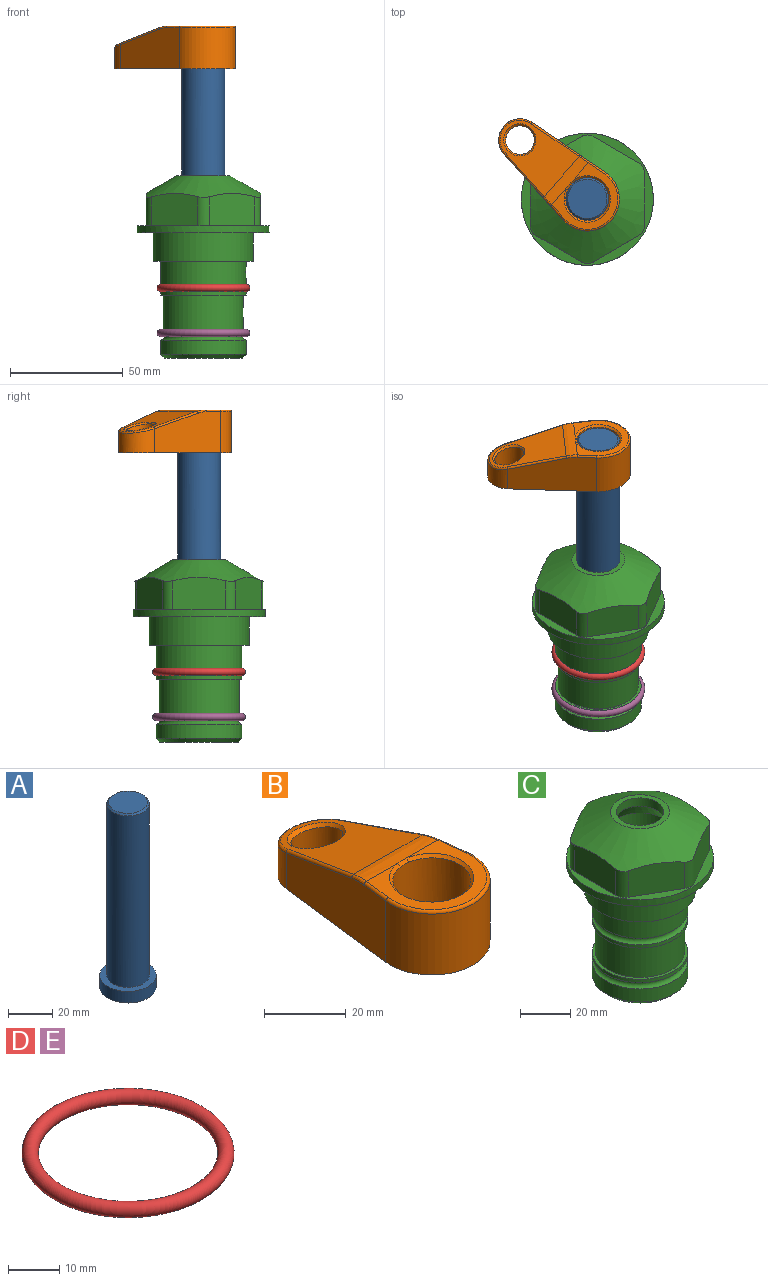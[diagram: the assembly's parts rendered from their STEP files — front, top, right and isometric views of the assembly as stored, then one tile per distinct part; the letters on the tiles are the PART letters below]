
ASSEMBLY  parts=5 mates=4
PART A: 6 faces, bbox 25.4x25.4x101.6 mm
  f0: plane 17.46x17.46mm, normal (0,0,1), area 239.5mm2, adj f5
  f1: plane 25.4x25.4mm, normal (0,0,-1), area 506.7mm2, adj f2
  f2: cylinder r=12.7mm len=25.4mm, axis (0,0,1), area 506.7mm2, adj f1,f3
  f3: plane 25.4x25.4mm, normal (0,0,1), area 221.7mm2, adj f2,f4
  f4: cylinder r=9.53mm len=94.46mm, axis (0,0,1), area 5653mm2, adj f3,f5
  f5: cone r=8.73mm half-angle=45deg, axis (0,0,-1), area 64.4mm2, adj f0,f4
PART B: 31 faces, bbox 31.7x65.5x19.8 mm
  f0: plane 39.12x18.26mm, normal (0.99,0.12,0), area 612.2mm2, adj f1,f4,f7,f11,f13,f15
  f1: cylinder r=9.53mm len=18.91mm, axis (0,0,-1), area 296.1mm2, adj f0,f2,f7,f17
  f2: plane 39.12x18.26mm, normal (-0.99,0.12,0), area 612.2mm2, adj f1,f4,f7,f12,f14,f16
  f3: cylinder r=6.35mm len=12.7mm, axis (0,0,-1), area 362.4mm2, adj f7,f18
  f4: cylinder r=14.29mm len=28.58mm, axis (0,0,-1), area 882.2mm2, adj f0,f2,f7,f10
  f5: cylinder r=9.53mm len=19.05mm, axis (0,0,-1), area 1092.6mm2, adj f7,f19,f20
  f6: plane 26.99x23.69mm, normal (0,0,1), area 216.2mm2, adj f9,f10,f11,f12,f19
  f7: plane 63.5x28.58mm, normal (0,0,-1), area 661.8mm2, adj f0,f1,f2,f3,f4,f5,f22,f23
  f8: plane 33.52x23.6mm, normal (0,0.26,0.97), area 486mm2, adj f9,f15,f16,f17,f18
  f9: cylinder r=19.05mm len=24.72mm, axis (1,0,0), area 120.4mm2, adj f6,f8,f13,f14,f20
  f10: torus R=13.49mm, axis (0,0,1), area 59mm2, adj f4,f6,f11,f12
  f11: cylinder r=0.79mm len=8.67mm, axis (0.12,-0.99,0), area 10.8mm2, adj f0,f6,f10,f13
  f12: cylinder r=0.79mm len=8.67mm, axis (0.12,0.99,0), area 10.8mm2, adj f2,f6,f10,f14
  f13: bspline ~4.95x1.42mm, area 6.1mm2, adj f0,f9,f11,f15
  f14: bspline ~4.95x1.42mm, area 6.1mm2, adj f2,f9,f12,f16
  f15: cylinder r=0.79mm len=25.95mm, axis (0.12,-0.96,0.26), area 32.9mm2, adj f0,f8,f13,f17
  f16: cylinder r=0.79mm len=25.95mm, axis (0.12,0.96,-0.26), area 32.9mm2, adj f2,f8,f14,f17
  f17: bspline ~18.91x8.38mm, area 30mm2, adj f1,f8,f15,f16
  f18: bspline ~14.29x14.29mm, area 48.3mm2, adj f3,f8
  f19: cone r=9.53mm half-angle=45deg, axis (0,0,1), area 66.5mm2, adj f5,f6,f20
  f20: bspline ~3.22x0.96mm, area 3.5mm2, adj f5,f9,f19
  f21: plane 2.75x2.72mm, normal (0,0,-1), area 2.9mm2, adj f23,f25,f28
  f22: plane 23.05x15.88mm, normal (-0.99,-0.12,0), area 323.6mm2, adj f7,f25,f26,f27,f28,f29
  f23: plane 23.05x15.88mm, normal (0.99,-0.12,0), area 323.6mm2, adj f7,f21,f25,f27,f28,f30
  f24: cylinder r=9.53mm len=10.69mm, axis (0,0,-1), area 114.7mm2, adj f7,f27,f29,f30
  f25: cylinder r=12.7mm len=20.59mm, axis (0,0,-1), area 381.1mm2, adj f7,f21,f22,f23,f26,f28
  f26: plane 2.75x2.72mm, normal (0,0,-1), area 2.9mm2, adj f22,f25,f28
  f27: plane 19.72x18.37mm, normal (0,-0.26,-0.97), area 291.8mm2, adj f22,f23,f24,f28,f29,f30
  f28: cylinder r=15.88mm len=19.92mm, axis (1,0,0), area 54.8mm2, adj f21,f22,f23,f25,f26,f27
  f29: cylinder r=1.59mm len=11mm, axis (0,0,-1), area 34.7mm2, adj f7,f22,f24,f27
  f30: cylinder r=1.59mm len=11mm, axis (0,0,-1), area 34.7mm2, adj f7,f23,f24,f27
PART C: 36 faces, bbox 58.7x58.7x81 mm
  f0: cylinder r=17.78mm len=35.56mm, axis (0,0,1), area 1670.8mm2, adj f23,f24,f31
  f1: cylinder r=19.05mm len=38.1mm, axis (0,0,1), area 1191.9mm2, adj f26,f27,f30
  f2: plane 58.66x58.66mm, normal (0,0,-1), area 1150.6mm2, adj f3,f28
  f3: cylinder r=29.33mm len=58.66mm, axis (0,0,-1), area 585.1mm2, adj f2,f4
  f4: plane 58.66x58.66mm, normal (0,0,1), area 475.9mm2, adj f3,f5,f6,f7,f8,f9,f10,f11
  f5: plane 20.32x14.34mm, normal (-0.5,0.87,0), area 324.4mm2, adj f4,f15,f16,f17
  f6: plane 20.32x14.34mm, normal (0.5,0.87,0), area 324.4mm2, adj f4,f14,f15,f17
  f7: plane 23.48x14.34mm, normal (1,0,0), area 324.4mm2, adj f4,f13,f14,f17
  f8: plane 20.32x14.34mm, normal (0.5,-0.87,0), area 324.4mm2, adj f4,f12,f13,f17
  f9: plane 20.32x14.34mm, normal (-0.5,-0.87,0), area 324.4mm2, adj f4,f11,f12,f17
  f10: plane 23.48x14.34mm, normal (-1,0,0), area 324.4mm2, adj f4,f11,f16,f17
  f11: cylinder r=5.08mm len=12.85mm, axis (0,0,-1), area 67.2mm2, adj f4,f9,f10,f17
  f12: cylinder r=5.08mm len=12.85mm, axis (0,0,-1), area 67.2mm2, adj f4,f8,f9,f17
  f13: cylinder r=5.08mm len=12.85mm, axis (0,0,-1), area 67.2mm2, adj f4,f7,f8,f17
  f14: cylinder r=5.08mm len=12.85mm, axis (0,0,-1), area 67.2mm2, adj f4,f6,f7,f17
  f15: cylinder r=5.08mm len=12.85mm, axis (0,0,-1), area 67.2mm2, adj f4,f5,f6,f17
  f16: cylinder r=5.08mm len=12.85mm, axis (0,0,-1), area 67.2mm2, adj f4,f5,f10,f17
  f17: cone r=11.73mm half-angle=60deg, axis (0,0,-1), area 2071.8mm2, adj f5,f6,f7,f8,f9,f10,f11,f12
  f18: plane 23.46x23.46mm, normal (0,0,1), area 147.4mm2, adj f17,f35
  f19: plane 34.93x34.93mm, normal (0,0,-1), area 958mm2, adj f29
  f20: cylinder r=19.05mm len=38.1mm, axis (0,0,1), area 760.1mm2, adj f21,f29
  f21: torus R=19.05mm, axis (0,0,1), area 565.3mm2, adj f20,f22
  f22: cylinder r=19.05mm len=38.1mm, axis (0,0,1), area 190mm2, adj f21,f23
  f23: plane 38.1x38.1mm, normal (0,0,1), area 146.9mm2, adj f0,f22
  f24: plane 38.1x38.1mm, normal (0,0,-1), area 146.9mm2, adj f0,f25
  f25: cylinder r=19.05mm len=38.1mm, axis (0,0,1), area 190mm2, adj f24,f26
  f26: torus R=19.05mm, axis (0,0,1), area 565.3mm2, adj f1,f25
  f27: plane 44.45x44.45mm, normal (0,0,-1), area 411.7mm2, adj f1,f28
  f28: cylinder r=22.23mm len=44.45mm, axis (0,0,1), area 1773.5mm2, adj f2,f27
  f29: cone r=19.05mm half-angle=45deg, axis (0,0,1), area 257.5mm2, adj f19,f20
  f30: cylinder r=3.17mm len=6.75mm, axis (-1,0,0), area 128mm2, adj f1,f33
  f31: cylinder r=3.17mm len=6.35mm, axis (-1,0,0), area 102.5mm2, adj f0,f33
  f32: plane 25.4x25.4mm, normal (0,0,1), area 506.7mm2, adj f33
  f33: cylinder r=12.7mm len=66.42mm, axis (0,0,-1), area 5236.2mm2, adj f30,f31,f32,f34
  f34: cone r=9.53mm half-angle=30deg, axis (0,0,-1), area 443.4mm2, adj f33,f35
  f35: cylinder r=9.53mm len=19.05mm, axis (0,0,-1), area 240.9mm2, adj f18,f34
PART D: 1 faces, bbox 44.7x44.7x3.2 mm
  f0: torus R=19.05mm, axis (0,0,1), area 1193.9mm2
PART E: same geometry as D
PLACE A rot(axis=(0,0,1),48.8deg) t=(-69.99,-42.13,35.89)mm
PLACE B rot(axis=(0,0,1),48.8deg) t=(-69.99,-42.13,36.69)mm
PLACE C t=(-69.99,-42.13,8.34)mm fixed
PLACE D t=(-69.99,-42.13,8.34)mm
PLACE E t=(-69.99,-42.13,-11.66)mm
MATE fastened C.f0 <-> E.f0  axis (0,0,1) through (-69.99,-42.13,-36.17)mm
MATE fastened A.f2 <-> B.f4  axis (0,0,1) through (-69.99,-42.13,99.39)mm
MATE fastened C.f0 <-> D.f0  axis (0,0,1) through (-69.99,-42.13,-16.17)mm
MATE cylindrical A.f2 <-> C.f0  axis (0,0,-1) through (-69.99,-42.13,-2.21)mm
